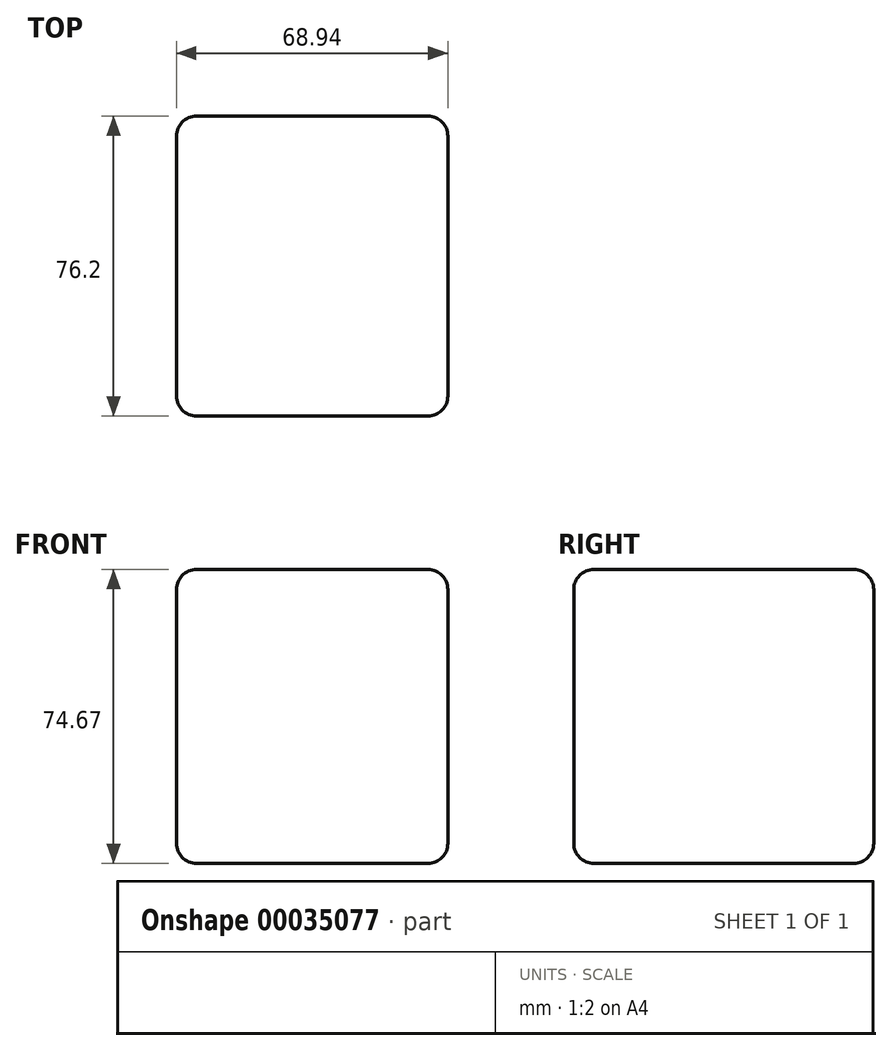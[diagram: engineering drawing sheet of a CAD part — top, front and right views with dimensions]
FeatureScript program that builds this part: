
annotation { "Feature Type Name" : "Feature", "Feature Type Description" : "" }
export const myFeature = defineFeature(function(context is Context, id is Id, definition is map)
    precondition{}
    {
        {
            var Q0;
            Q0=qCreatedBy(makeId("Front.planeOp"),FACE);
            var sketch = newSketch(context, id + "F0", { "sketchPlane" : qUnion([Q0])});
            skLineSegment(sketch, "E0.bottom", {"start": v(34.82, 36.86) * mm, "end": v(-34.12, 36.86) * mm});
            skLineSegment(sketch, "E0.top", {"start": v(34.82, -37.8) * mm, "end": v(-34.12, -37.8) * mm});
            skLineSegment(sketch, "E0.left", {"start": v(34.82, 36.86) * mm, "end": v(34.82, -37.8) * mm});
            skLineSegment(sketch, "E0.right", {"start": v(-34.12, 36.86) * mm, "end": v(-34.12, -37.8) * mm});
            skSolve(sketch);
        }
        {
            var Q0;
            Q0 = qSketchRegion(id + "F0", true);
            var Q1;
            Q1=makeQuery(id+"F0.imprint","IMPRINT",FACE,{"disambiguationData":[TD([[makeQuery(id+"F0.imprint","IMPRINT",EDGE,{"derivedFrom":sQuery(id+"F0.wireOp",EDGE,"E0.bottom")}),1.0]])]});
            extrude(context, id + "F1", {"entities" : qUnion([Q0, Q1]), "depth" : 76.2 * mm});
        }
        {
            var Q0;
            Q0=makeQuery(id+"F1.opExtrude","CAP_FACE",FACE,{"disambiguationData":[OSD([sQuery(id+"F0.wireOp",EDGE,"E0.bottom"),sQuery(id+"F0.wireOp",EDGE,"E0.top"),sQuery(id+"F0.wireOp",EDGE,"E0.left"),sQuery(id+"F0.wireOp",EDGE,"E0.right")])],"isStart":false});
            var Q1;
            Q1=makeQuery(id+"F1.opExtrude","CAP_EDGE",EDGE,{"disambiguationData":[OSD([sQuery(id+"F0.wireOp",EDGE,"E0.bottom")])],"isStart":false});
            fillet(context, id + "F2", {"entities" : qUnion([Q0, Q1]), "radius" : 5.08 * mm, "tangentPropagation" : true, "allowEdgeOverflow" : false});
        }
        {
            var Q0;
            Q0=makeQuery(id+"F1.opExtrude","CAP_EDGE",EDGE,{"disambiguationData":[OSD([sQuery(id+"F0.wireOp",EDGE,"E0.left")])],"isStart":true});
            fillet(context, id + "F3", {"entities" : qUnion([Q0]), "radius" : 5.08 * mm, "tangentPropagation" : true, "allowEdgeOverflow" : false});
        }
        {
            var Q0;
            Q0=makeQuery(id+"F1.opExtrude","CAP_EDGE",EDGE,{"disambiguationData":[OSD([sQuery(id+"F0.wireOp",EDGE,"E0.right")])],"isStart":true});
            fillet(context, id + "F4", {"entities" : qUnion([Q0]), "radius" : 5.08 * mm, "tangentPropagation" : true, "allowEdgeOverflow" : false});
        }
        {
            var Q0;
            Q0=makeQuery(id+"F1.opExtrude","SWEPT_EDGE",EDGE,{"disambiguationData":[OSD([sQuery(id+"F0.wireOp",EDGE,"E0.bottom"),sQuery(id+"F0.wireOp",EDGE,"E0.left")])]});
            fillet(context, id + "F5", {"entities" : qUnion([Q0]), "radius" : 5.08 * mm, "tangentPropagation" : true, "allowEdgeOverflow" : false});
        }
        {
            var Q0;
            Q0=makeQuery(id+"F1.opExtrude","CAP_EDGE",EDGE,{"disambiguationData":[OSD([sQuery(id+"F0.wireOp",EDGE,"E0.top")])],"isStart":true});
            fillet(context, id + "F6", {"entities" : qUnion([Q0]), "radius" : 5.08 * mm, "tangentPropagation" : true, "allowEdgeOverflow" : false});
        }
    });
